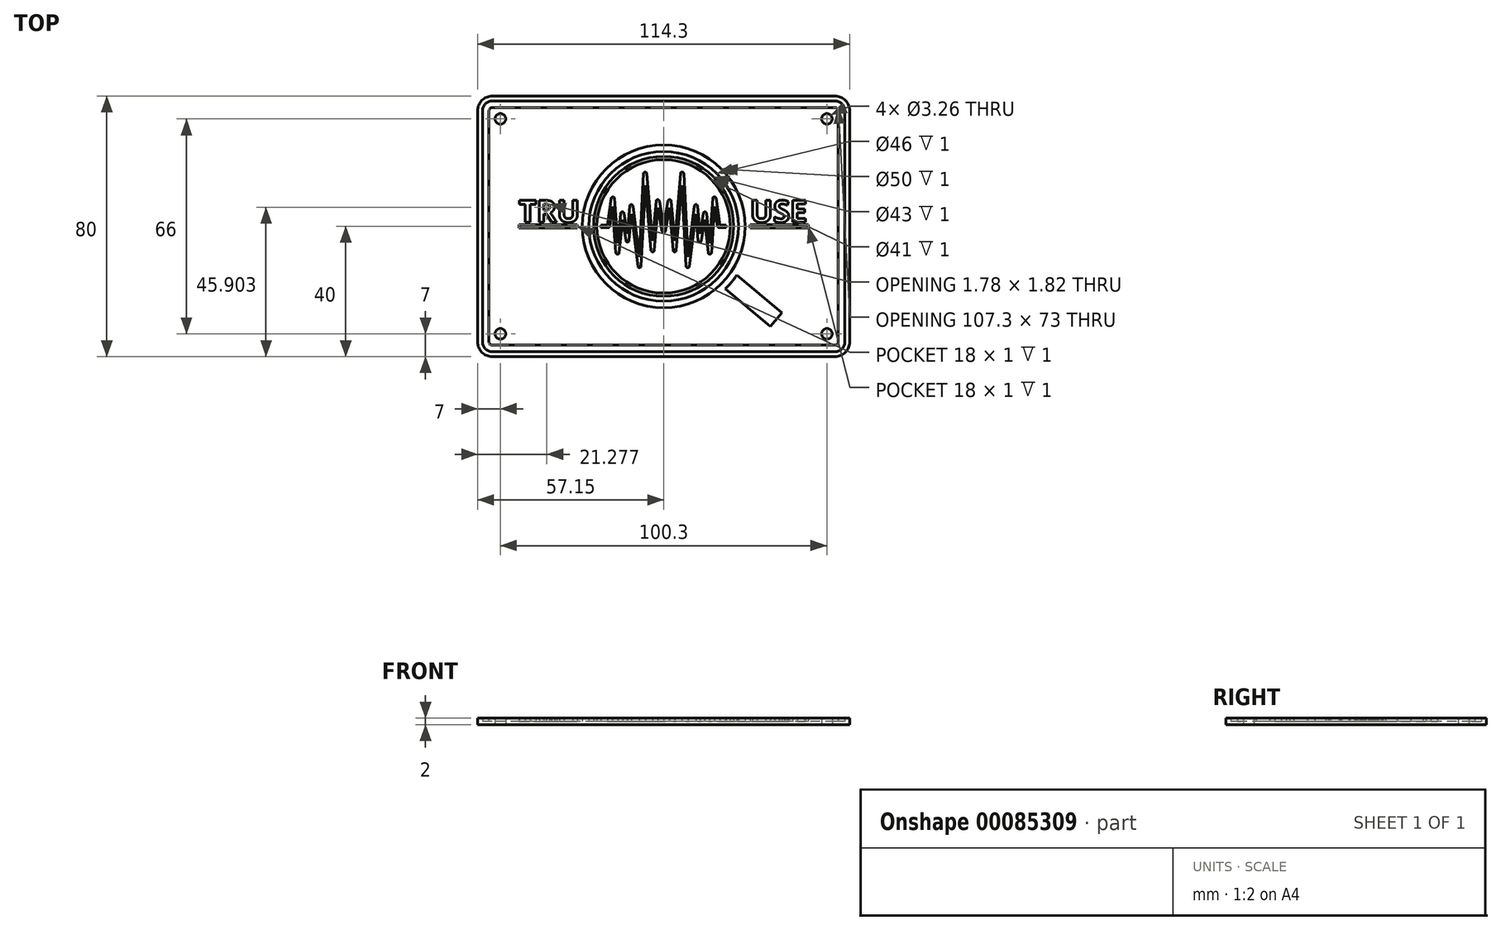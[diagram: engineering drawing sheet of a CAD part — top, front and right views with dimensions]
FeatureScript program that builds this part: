
annotation { "Feature Type Name" : "Feature", "Feature Type Description" : "" }
export const myFeature = defineFeature(function(context is Context, id is Id, definition is map)
    precondition{}
    {
        {
            var Q0;
            Q0=qCreatedBy(makeId("Front.planeOp"),FACE);
            var sketch = newSketch(context, id + "F0", { "sketchPlane" : qUnion([Q0])});
            skLineSegment(sketch, "E0.bottom", {"start": v(-57.15, 0) * mm, "end": v(57.15, 0) * mm});
            skLineSegment(sketch, "E0.top", {"start": v(-57.15, 2) * mm, "end": v(57.15, 2) * mm});
            skLineSegment(sketch, "E0.left", {"start": v(-57.15, 0) * mm, "end": v(-57.15, 2) * mm});
            skLineSegment(sketch, "E0.right", {"start": v(57.15, 0) * mm, "end": v(57.15, 2) * mm});
            skSolve(sketch);
        }
        {
            var Q0;
            Q0=makeQuery(id+"F0.imprint","IMPRINT",FACE,{"disambiguationData":[TD([[makeQuery(id+"F0.imprint","IMPRINT",EDGE,{"derivedFrom":sQuery(id+"F0.wireOp",EDGE,"E0.bottom")}),1.0]])]});
            extrude(context, id + "F1", {"entities" : qUnion([Q0]), "endBound" : BoundingType.SYMMETRIC, "depth" : 80 * mm});
        }
        {
            var Q0;
            Q0=qCreatedBy(makeId("Top.planeOp"),FACE);
            cPlane(context, id + "F2", {"entities" : qUnion([Q0]), "cplaneType" : CPlaneType.OFFSET, "offset" : 1 * mm, "width" : 150 * mm, "height" : 150 * mm});
        }
        {
            var Q0;
            Q0=qCreatedBy(id+"F2.planeOp",FACE);
            var sketch = newSketch(context, id + "F3", { "sketchPlane" : qUnion([Q0])});
            skCircle(sketch, "E1", {"center": v(0, 0) * mm, "radius": 25 * mm});
            skLineSegment(sketch, "E2.bottom", {"start": v(-44.5, -0.5) * mm, "end": v(-26.5, -0.5) * mm});
            skLineSegment(sketch, "E2.top", {"start": v(-44.5, 0.5) * mm, "end": v(-26.5, 0.5) * mm});
            skLineSegment(sketch, "E2.left", {"start": v(-44.5, -0.5) * mm, "end": v(-44.5, 0.5) * mm});
            skLineSegment(sketch, "E2.right", {"start": v(-26.5, -0.5) * mm, "end": v(-26.5, 0.5) * mm});
            skPoint(sketch, "E2.middle", {"position": v(-35.5, 0) * mm});
            skLineSegment(sketch, "E3.MirrorCS", {"start": v(44.5, 0.5) * mm, "end": v(26.5, 0.5) * mm});
            skLineSegment(sketch, "E4.MirrorCS", {"start": v(44.5, -0.5) * mm, "end": v(26.5, -0.5) * mm});
            skLineSegment(sketch, "E5.MirrorCS", {"start": v(26.5, -0.5) * mm, "end": v(26.5, 0.5) * mm});
            skLineSegment(sketch, "E6.MirrorCS", {"start": v(44.5, -0.5) * mm, "end": v(44.5, 0.5) * mm});
            skCircle(sketch, "E7", {"center": v(0, 0) * mm, "radius": 23 * mm});
            skSolve(sketch);
        }
        {
            var Q0;
            Q0=qSketchRegion(id+"F3",true);
            extrude(context, id + "F4", {"entities" : qUnion([Q0]), "depth" : 1 * mm});
        }
        {
            var Q0;
            Q0=qCreatedBy(id+"F2.planeOp",FACE);
            var sketch = newSketch(context, id + "F5", { "sketchPlane" : qUnion([Q0])});
            skCircle(sketch, "E8", {"center": v(0, 0) * mm, "radius": 21.5 * mm});
            skCircle(sketch, "E9", {"center": v(0, 0) * mm, "radius": 20.5 * mm});
            skSolve(sketch);
        }
        {
            var Q0;
            Q0=qSketchRegion(id+"F5",true);
            extrude(context, id + "F6", {"entities" : qUnion([Q0]), "depth" : 1 * mm});
        }
        {
            var Q0;
            Q0=qCreatedBy(id+"F2.planeOp",FACE);
            var sketch = newSketch(context, id + "F7", { "sketchPlane" : qUnion([Q0])});
            skLineSegment(sketch, "E10.0", {"start": v(19, -19.19) * mm, "end": v(32.78, -30.76) * mm});
            skLineSegment(sketch, "E11.0", {"start": v(22.49, -14.94) * mm, "end": v(36.32, -26.55) * mm});
            skLineSegment(sketch, "E12", {"start": v(36.32, -26.55) * mm, "end": v(32.78, -30.76) * mm});
            skArc(sketch, "E13", {"start": v(19, -19.19) * mm, "mid": v(20.85, -17.15) * mm, "end": v(22.49, -14.94) * mm});
            skSolve(sketch);
        }
        {
            var Q0;
            Q0=qSketchRegion(id+"F7",true);
            extrude(context, id + "F8", {"entities" : qUnion([Q0]), "depth" : 1 * mm});
        }
        {
            var Q0;
            Q0=qCreatedBy(id+"F2.planeOp",FACE);
            var sketch = newSketch(context, id + "F9", { "sketchPlane" : qUnion([Q0])});
            skText(sketch, "E14", { "text": "TRU", "fontName": "OpenSans-Bold.ttf"});
            skText(sketch, "E15", { "text": "USE", "fontName": "OpenSans-Bold.ttf"});
            const initialGuessF9  = {"E14": [-0.0445, 0.00125, 1, 0, 0.00679], "E15": [0.0265, 0.00125, 1, 0, 0.00678]};
            skSetInitialGuess(sketch, initialGuessF9);
            skSolve(sketch);
        }
        {
            var Q0;
            Q0=qSketchRegion(id+"F9",true);
            extrude(context, id + "F10", {"entities" : qUnion([Q0]), "depth" : 1 * mm});
        }
        {
            var Q0;
            Q0=qCreatedBy(id+"F2.planeOp",FACE);
            var sketch = newSketch(context, id + "F11", { "sketchPlane" : qUnion([Q0])});
            skPoint(sketch, "E16.middle", {"position": v(0, 0) * mm});
            skLineSegment(sketch, "E17.bottom", {"start": v(52.65, 38.5) * mm, "end": v(-52.65, 38.5) * mm});
            skLineSegment(sketch, "E17.top", {"start": v(52.65, -38.5) * mm, "end": v(-52.65, -38.5) * mm});
            skLineSegment(sketch, "E17.left", {"start": v(55.65, 35.5) * mm, "end": v(55.65, -35.5) * mm});
            skLineSegment(sketch, "E17.right", {"start": v(-55.65, 35.5) * mm, "end": v(-55.65, -35.5) * mm});
            skLineSegment(sketch, "E18.bottom", {"start": v(52.65, 36.5) * mm, "end": v(-52.65, 36.5) * mm});
            skLineSegment(sketch, "E18.top", {"start": v(52.65, -36.5) * mm, "end": v(-52.65, -36.5) * mm});
            skLineSegment(sketch, "E18.left", {"start": v(53.65, 35.5) * mm, "end": v(53.65, -35.5) * mm});
            skLineSegment(sketch, "E18.right", {"start": v(-53.65, 35.5) * mm, "end": v(-53.65, -35.5) * mm});
            skPoint(sketch, "E19.visualSharp", {"position": v(-55.65, 38.5) * mm});
            skArc(sketch, "E19.filletArc", {"start": v(-52.65, 38.5) * mm, "mid": v(-54.77, 37.62) * mm, "end": v(-55.65, 35.5) * mm});
            skPoint(sketch, "E20.visualSharp", {"position": v(55.65, 38.5) * mm});
            skArc(sketch, "E20.filletArc", {"start": v(55.65, 35.5) * mm, "mid": v(54.77, 37.62) * mm, "end": v(52.65, 38.5) * mm});
            skPoint(sketch, "E21.visualSharp", {"position": v(55.65, -38.5) * mm});
            skArc(sketch, "E21.filletArc", {"start": v(52.65, -38.5) * mm, "mid": v(54.77, -37.62) * mm, "end": v(55.65, -35.5) * mm});
            skPoint(sketch, "E22.visualSharp", {"position": v(-55.65, -38.5) * mm});
            skArc(sketch, "E22.filletArc", {"start": v(-55.65, -35.5) * mm, "mid": v(-54.77, -37.62) * mm, "end": v(-52.65, -38.5) * mm});
            skPoint(sketch, "E23.visualSharp", {"position": v(53.65, 36.5) * mm});
            skArc(sketch, "E23.filletArc", {"start": v(53.65, 35.5) * mm, "mid": v(53.36, 36.2) * mm, "end": v(52.65, 36.5) * mm});
            skPoint(sketch, "E24.visualSharp", {"position": v(-53.65, 36.5) * mm});
            skArc(sketch, "E24.filletArc", {"start": v(-52.65, 36.5) * mm, "mid": v(-53.36, 36.2) * mm, "end": v(-53.65, 35.5) * mm});
            skPoint(sketch, "E25.visualSharp", {"position": v(-53.65, -36.5) * mm});
            skArc(sketch, "E25.filletArc", {"start": v(-53.65, -35.5) * mm, "mid": v(-53.36, -36.2) * mm, "end": v(-52.65, -36.5) * mm});
            skPoint(sketch, "E26.visualSharp", {"position": v(53.65, -36.5) * mm});
            skArc(sketch, "E26.filletArc", {"start": v(52.65, -36.5) * mm, "mid": v(53.36, -36.2) * mm, "end": v(53.65, -35.5) * mm});
            skSolve(sketch);
        }
        {
            var Q0;
            Q0=qSketchRegion(id+"F11",true);
            extrude(context, id + "F12", {"entities" : qUnion([Q0]), "depth" : 1 * mm});
        }
        {
            var Q0;
            Q0=qCreatedBy(id+"F2.planeOp",FACE);
            var sketch = newSketch(context, id + "F13", { "sketchPlane" : qUnion([Q0])});
            skLineSegment(sketch, "E27.bottom", {"start": v(-17.03, -0.38) * mm, "end": v(-19.25, -0.37) * mm});
            skLineSegment(sketch, "E27.top", {"start": v(-17.25, 0.38) * mm, "end": v(-19.25, 0.38) * mm});
            skLineSegment(sketch, "E27.right", {"start": v(-19.25, -0.37) * mm, "end": v(-19.25, 0.38) * mm});
            skPoint(sketch, "E27.middle", {"position": v(-18.25, 0) * mm});
            skLineSegment(sketch, "E28", {"start": v(-17.25, 0.37) * mm, "end": v(-16.09, 8.62) * mm});
            skLineSegment(sketch, "E29.0", {"start": v(-16.53, 0.06) * mm, "end": v(-15.68, 6.16) * mm});
            skPoint(sketch, "E27.left.start.orphan", {"position": v(-17.25, -0.38) * mm});
            skPoint(sketch, "E30.visualSharp", {"position": v(-16.6, -0.38) * mm});
            skArc(sketch, "E30.filletArc", {"start": v(-17.03, -0.38) * mm, "mid": v(-16.7, -0.25) * mm, "end": v(-16.53, 0.06) * mm});
            skLineSegment(sketch, "E31", {"start": v(-15.68, 6.16) * mm, "end": v(-14.68, -8.1) * mm});
            skLineSegment(sketch, "E32.0", {"start": v(-15.1, 8.58) * mm, "end": v(-14.13, -5.19) * mm});
            skPoint(sketch, "E33.visualSharp", {"position": v(-15.43, 13.33) * mm});
            skArc(sketch, "E33.filletArc", {"start": v(-15.1, 8.58) * mm, "mid": v(-15.58, 9.05) * mm, "end": v(-16.09, 8.62) * mm});
            skLineSegment(sketch, "E34", {"start": v(-14.13, -5.19) * mm, "end": v(-13.16, 4) * mm});
            skLineSegment(sketch, "E35.0", {"start": v(-13.68, -8.1) * mm, "end": v(-12.62, 2.03) * mm});
            skLineSegment(sketch, "E36", {"start": v(-12.62, 2.03) * mm, "end": v(-11.6, -4.4) * mm});
            skLineSegment(sketch, "E37.0", {"start": v(-12.17, 4.02) * mm, "end": v(-11.18, -2.27) * mm});
            skLineSegment(sketch, "E38", {"start": v(-11.18, -2.27) * mm, "end": v(-10.43, 6.22) * mm});
            skLineSegment(sketch, "E39.0", {"start": v(-10.6, -4.37) * mm, "end": v(-9.9, 3.78) * mm});
            skLineSegment(sketch, "E40", {"start": v(-9.9, 3.78) * mm, "end": v(-7.92, -12.26) * mm});
            skLineSegment(sketch, "E41.0", {"start": v(-9.44, 6.24) * mm, "end": v(-7.53, -9.33) * mm});
            skLineSegment(sketch, "E42", {"start": v(-7.53, -9.33) * mm, "end": v(-6.19, 16.22) * mm});
            skLineSegment(sketch, "E43.0", {"start": v(-6.93, -12.22) * mm, "end": v(-5.63, 12.61) * mm});
            skLineSegment(sketch, "E44", {"start": v(-5.63, 12.61) * mm, "end": v(-3.88, -7.38) * mm});
            skLineSegment(sketch, "E45.0", {"start": v(-5.2, 16.24) * mm, "end": v(-3.38, -4.47) * mm});
            skLineSegment(sketch, "E46", {"start": v(-3.38, -4.47) * mm, "end": v(-2.31, 7.74) * mm});
            skLineSegment(sketch, "E47.0", {"start": v(-2.88, -7.38) * mm, "end": v(-1.73, 5.74) * mm});
            skLineSegment(sketch, "E48", {"start": v(0, 12.7) * mm, "end": v(0, -16.33) * mm, "construction": true});
            skLineSegment(sketch, "E49", {"start": v(-1.73, 5.74) * mm, "end": v(-0.5, -1.53) * mm});
            skLineSegment(sketch, "E50.0", {"start": v(-1.32, 7.78) * mm, "end": v(0, 0.04) * mm});
            skPoint(sketch, "E51.visualSharp", {"position": v(-14.28, -13.8) * mm});
            skArc(sketch, "E51.filletArc", {"start": v(-14.68, -8.1) * mm, "mid": v(-14.19, -8.56) * mm, "end": v(-13.68, -8.1) * mm});
            skPoint(sketch, "E52.visualSharp", {"position": v(-12.77, 7.78) * mm});
            skArc(sketch, "E52.filletArc", {"start": v(-12.17, 4.02) * mm, "mid": v(-12.68, 4.45) * mm, "end": v(-13.16, 4) * mm});
            skPoint(sketch, "E53.visualSharp", {"position": v(-10.96, -8.42) * mm});
            skArc(sketch, "E53.filletArc", {"start": v(-11.6, -4.4) * mm, "mid": v(-11.09, -4.82) * mm, "end": v(-10.6, -4.37) * mm});
            skPoint(sketch, "E54.visualSharp", {"position": v(-10.02, 10.96) * mm});
            skArc(sketch, "E54.filletArc", {"start": v(-9.44, 6.24) * mm, "mid": v(-9.94, 6.67) * mm, "end": v(-10.43, 6.22) * mm});
            skPoint(sketch, "E55.visualSharp", {"position": v(-7.23, -17.93) * mm});
            skArc(sketch, "E55.filletArc", {"start": v(-7.92, -12.26) * mm, "mid": v(-7.4, -12.7) * mm, "end": v(-6.93, -12.22) * mm});
            skPoint(sketch, "E56.visualSharp", {"position": v(-5.81, 23.36) * mm});
            skArc(sketch, "E56.filletArc", {"start": v(-5.2, 16.24) * mm, "mid": v(-5.7, 16.7) * mm, "end": v(-6.19, 16.22) * mm});
            skPoint(sketch, "E57.visualSharp", {"position": v(-3.38, -13.07) * mm});
            skArc(sketch, "E57.filletArc", {"start": v(-3.88, -7.38) * mm, "mid": v(-3.38, -7.84) * mm, "end": v(-2.88, -7.38) * mm});
            skPoint(sketch, "E58.visualSharp", {"position": v(-1.97, 11.61) * mm});
            skArc(sketch, "E58.filletArc", {"start": v(-1.32, 7.78) * mm, "mid": v(-1.83, 8.2) * mm, "end": v(-2.31, 7.74) * mm});
            skArc(sketch, "E59.MirrorCS", {"start": v(17.03, -0.38) * mm, "mid": v(16.7, -0.25) * mm, "end": v(16.53, 0.06) * mm});
            skArc(sketch, "E60.MirrorCS", {"start": v(5.2, 16.24) * mm, "mid": v(5.7, 16.7) * mm, "end": v(6.19, 16.22) * mm});
            skArc(sketch, "E61.MirrorCS", {"start": v(1.32, 7.78) * mm, "mid": v(1.83, 8.2) * mm, "end": v(2.31, 7.74) * mm});
            skArc(sketch, "E62.MirrorCS", {"start": v(3.88, -7.38) * mm, "mid": v(3.38, -7.84) * mm, "end": v(2.88, -7.38) * mm});
            skArc(sketch, "E63.MirrorCS", {"start": v(14.68, -8.1) * mm, "mid": v(14.19, -8.56) * mm, "end": v(13.68, -8.1) * mm});
            skArc(sketch, "E64.MirrorCS", {"start": v(11.6, -4.4) * mm, "mid": v(11.09, -4.82) * mm, "end": v(10.6, -4.37) * mm});
            skArc(sketch, "E65.MirrorCS", {"start": v(9.44, 6.24) * mm, "mid": v(9.94, 6.67) * mm, "end": v(10.43, 6.22) * mm});
            skArc(sketch, "E66.MirrorCS", {"start": v(15.1, 8.58) * mm, "mid": v(15.58, 9.05) * mm, "end": v(16.09, 8.62) * mm});
            skArc(sketch, "E67.MirrorCS", {"start": v(12.17, 4.02) * mm, "mid": v(12.68, 4.45) * mm, "end": v(13.16, 4) * mm});
            skArc(sketch, "E68.MirrorCS", {"start": v(7.92, -12.26) * mm, "mid": v(7.4, -12.7) * mm, "end": v(6.93, -12.22) * mm});
            skLineSegment(sketch, "E69.MirrorCS", {"start": v(19.25, -0.37) * mm, "end": v(19.25, 0.38) * mm});
            skLineSegment(sketch, "E70.MirrorCS", {"start": v(17.03, -0.38) * mm, "end": v(19.25, -0.37) * mm});
            skPoint(sketch, "E71.MirrorP", {"position": v(16.6, -0.38) * mm});
            skLineSegment(sketch, "E72.MirrorCS", {"start": v(17.25, 0.38) * mm, "end": v(19.25, 0.38) * mm});
            skPoint(sketch, "E73.MirrorP", {"position": v(17.25, -0.38) * mm});
            skPoint(sketch, "E74.MirrorP", {"position": v(18.25, 0) * mm});
            skLineSegment(sketch, "E75.MirrorCS", {"start": v(7.53, -9.33) * mm, "end": v(6.19, 16.22) * mm});
            skPoint(sketch, "E76.MirrorP", {"position": v(12.77, 7.78) * mm});
            skLineSegment(sketch, "E77.MirrorCS", {"start": v(3.38, -4.47) * mm, "end": v(2.31, 7.74) * mm});
            skLineSegment(sketch, "E78.MirrorCS", {"start": v(12.17, 4.02) * mm, "end": v(11.18, -2.27) * mm});
            skLineSegment(sketch, "E79.MirrorCS", {"start": v(1.73, 5.74) * mm, "end": v(0.5, -1.53) * mm});
            skPoint(sketch, "E80.MirrorP", {"position": v(14.28, -13.8) * mm});
            skLineSegment(sketch, "E81.MirrorCS", {"start": v(1.32, 7.78) * mm, "end": v(0, 0.04) * mm});
            skLineSegment(sketch, "E82.MirrorCS", {"start": v(10.6, -4.37) * mm, "end": v(9.9, 3.78) * mm});
            skLineSegment(sketch, "E83.MirrorCS", {"start": v(9.9, 3.78) * mm, "end": v(7.92, -12.26) * mm});
            skPoint(sketch, "E84.MirrorP", {"position": v(10.96, -8.42) * mm});
            skLineSegment(sketch, "E85.MirrorCS", {"start": v(9.44, 6.24) * mm, "end": v(7.53, -9.33) * mm});
            skLineSegment(sketch, "E86.MirrorCS", {"start": v(2.88, -7.38) * mm, "end": v(1.73, 5.74) * mm});
            skLineSegment(sketch, "E87.MirrorCS", {"start": v(12.62, 2.03) * mm, "end": v(11.6, -4.4) * mm});
            skPoint(sketch, "E88.MirrorP", {"position": v(1.97, 11.61) * mm});
            skPoint(sketch, "E89.MirrorP", {"position": v(3.38, -13.07) * mm});
            skPoint(sketch, "E90.MirrorP", {"position": v(15.43, 13.33) * mm});
            skPoint(sketch, "E91.MirrorP", {"position": v(10.02, 10.96) * mm});
            skLineSegment(sketch, "E92.MirrorCS", {"start": v(5.2, 16.24) * mm, "end": v(3.38, -4.47) * mm});
            skLineSegment(sketch, "E93.MirrorCS", {"start": v(17.25, 0.37) * mm, "end": v(16.09, 8.62) * mm});
            skLineSegment(sketch, "E94.MirrorCS", {"start": v(5.63, 12.61) * mm, "end": v(3.88, -7.38) * mm});
            skLineSegment(sketch, "E95.MirrorCS", {"start": v(14.13, -5.19) * mm, "end": v(13.16, 4) * mm});
            skLineSegment(sketch, "E96.MirrorCS", {"start": v(13.68, -8.1) * mm, "end": v(12.62, 2.03) * mm});
            skLineSegment(sketch, "E97.MirrorCS", {"start": v(15.68, 6.16) * mm, "end": v(14.68, -8.1) * mm});
            skLineSegment(sketch, "E98.MirrorCS", {"start": v(6.93, -12.22) * mm, "end": v(5.63, 12.61) * mm});
            skLineSegment(sketch, "E99.MirrorCS", {"start": v(15.1, 8.58) * mm, "end": v(14.13, -5.19) * mm});
            skLineSegment(sketch, "E100.MirrorCS", {"start": v(16.53, 0.06) * mm, "end": v(15.68, 6.16) * mm});
            skLineSegment(sketch, "E101.MirrorCS", {"start": v(11.18, -2.27) * mm, "end": v(10.43, 6.22) * mm});
            skPoint(sketch, "E102.visualSharp", {"position": v(0, -4.42) * mm});
            skArc(sketch, "E102.filletArc", {"start": v(-0.5, -1.53) * mm, "mid": v(0, -1.95) * mm, "end": v(0.5, -1.53) * mm});
            skSolve(sketch);
        }
        {
            var Q0;
            Q0=qSketchRegion(id+"F13",true);
            extrude(context, id + "F14", {"entities" : qUnion([Q0]), "depth" : 1 * mm});
        }
        {
            var Q0;
            Q0=makeQuery(id+"F1.opExtrude","CAP_EDGE",EDGE,{"disambiguationData":[OSD([sQuery(id+"F0.wireOp",EDGE,"E0.right")])],"isStart":true});
            var Q1;
            Q1=makeQuery(id+"F1.opExtrude","CAP_EDGE",EDGE,{"disambiguationData":[OSD([sQuery(id+"F0.wireOp",EDGE,"E0.right")])],"isStart":false});
            var Q2;
            Q2=makeQuery(id+"F1.opExtrude","CAP_EDGE",EDGE,{"disambiguationData":[OSD([sQuery(id+"F0.wireOp",EDGE,"E0.left")])],"isStart":false});
            var Q3;
            Q3=makeQuery(id+"F1.opExtrude","CAP_EDGE",EDGE,{"disambiguationData":[OSD([sQuery(id+"F0.wireOp",EDGE,"E0.left")])],"isStart":true});
            fillet(context, id + "F15", {"entities" : qUnion([Q0, Q1, Q2, Q3]), "radius" : 4.5 * mm, "tangentPropagation" : true, "allowEdgeOverflow" : false});
        }
        {
            var Q0;
            Q0=makeQuery(id+"F14.opExtrude","SWEPT_BODY",BODY,{"disambiguationData":[OSD([sQuery(id+"F13.wireOp",EDGE,"E27.bottom"),sQuery(id+"F13.wireOp",EDGE,"E27.top"),sQuery(id+"F13.wireOp",EDGE,"E27.right"),sQuery(id+"F13.wireOp",EDGE,"E28"),sQuery(id+"F13.wireOp",EDGE,"E29.0"),sQuery(id+"F13.wireOp",EDGE,"E30.filletArc"),sQuery(id+"F13.wireOp",EDGE,"E31"),sQuery(id+"F13.wireOp",EDGE,"E32.0"),sQuery(id+"F13.wireOp",EDGE,"E33.filletArc"),sQuery(id+"F13.wireOp",EDGE,"E34"),sQuery(id+"F13.wireOp",EDGE,"E35.0"),sQuery(id+"F13.wireOp",EDGE,"E36"),sQuery(id+"F13.wireOp",EDGE,"E37.0"),sQuery(id+"F13.wireOp",EDGE,"E38"),sQuery(id+"F13.wireOp",EDGE,"E39.0"),sQuery(id+"F13.wireOp",EDGE,"E40"),sQuery(id+"F13.wireOp",EDGE,"E41.0"),sQuery(id+"F13.wireOp",EDGE,"E42"),sQuery(id+"F13.wireOp",EDGE,"E43.0"),sQuery(id+"F13.wireOp",EDGE,"E44"),sQuery(id+"F13.wireOp",EDGE,"E45.0"),sQuery(id+"F13.wireOp",EDGE,"E46"),sQuery(id+"F13.wireOp",EDGE,"E47.0"),sQuery(id+"F13.wireOp",EDGE,"E49"),sQuery(id+"F13.wireOp",EDGE,"E50.0"),sQuery(id+"F13.wireOp",EDGE,"E51.filletArc"),sQuery(id+"F13.wireOp",EDGE,"E52.filletArc"),sQuery(id+"F13.wireOp",EDGE,"E53.filletArc"),sQuery(id+"F13.wireOp",EDGE,"E54.filletArc"),sQuery(id+"F13.wireOp",EDGE,"E55.filletArc"),sQuery(id+"F13.wireOp",EDGE,"E56.filletArc"),sQuery(id+"F13.wireOp",EDGE,"E57.filletArc"),sQuery(id+"F13.wireOp",EDGE,"E58.filletArc"),sQuery(id+"F13.wireOp",EDGE,"E59.MirrorCS"),sQuery(id+"F13.wireOp",EDGE,"E60.MirrorCS"),sQuery(id+"F13.wireOp",EDGE,"E61.MirrorCS"),sQuery(id+"F13.wireOp",EDGE,"E62.MirrorCS"),sQuery(id+"F13.wireOp",EDGE,"E63.MirrorCS"),sQuery(id+"F13.wireOp",EDGE,"E64.MirrorCS"),sQuery(id+"F13.wireOp",EDGE,"E65.MirrorCS"),sQuery(id+"F13.wireOp",EDGE,"E66.MirrorCS"),sQuery(id+"F13.wireOp",EDGE,"E67.MirrorCS"),sQuery(id+"F13.wireOp",EDGE,"E68.MirrorCS"),sQuery(id+"F13.wireOp",EDGE,"E69.MirrorCS"),sQuery(id+"F13.wireOp",EDGE,"E70.MirrorCS"),sQuery(id+"F13.wireOp",EDGE,"E72.MirrorCS"),sQuery(id+"F13.wireOp",EDGE,"E75.MirrorCS"),sQuery(id+"F13.wireOp",EDGE,"E77.MirrorCS"),sQuery(id+"F13.wireOp",EDGE,"E78.MirrorCS"),sQuery(id+"F13.wireOp",EDGE,"E79.MirrorCS"),sQuery(id+"F13.wireOp",EDGE,"E81.MirrorCS"),sQuery(id+"F13.wireOp",EDGE,"E82.MirrorCS"),sQuery(id+"F13.wireOp",EDGE,"E83.MirrorCS"),sQuery(id+"F13.wireOp",EDGE,"E85.MirrorCS"),sQuery(id+"F13.wireOp",EDGE,"E86.MirrorCS"),sQuery(id+"F13.wireOp",EDGE,"E87.MirrorCS"),sQuery(id+"F13.wireOp",EDGE,"E92.MirrorCS"),sQuery(id+"F13.wireOp",EDGE,"E93.MirrorCS"),sQuery(id+"F13.wireOp",EDGE,"E94.MirrorCS"),sQuery(id+"F13.wireOp",EDGE,"E95.MirrorCS"),sQuery(id+"F13.wireOp",EDGE,"E96.MirrorCS"),sQuery(id+"F13.wireOp",EDGE,"E97.MirrorCS"),sQuery(id+"F13.wireOp",EDGE,"E98.MirrorCS"),sQuery(id+"F13.wireOp",EDGE,"E99.MirrorCS"),sQuery(id+"F13.wireOp",EDGE,"E100.MirrorCS"),sQuery(id+"F13.wireOp",EDGE,"E101.MirrorCS"),sQuery(id+"F13.wireOp",EDGE,"E102.filletArc")])]});
            var Q1;
            Q1=makeQuery(id+"F1.opExtrude","SWEPT_BODY",BODY,{"disambiguationData":[OSD([sQuery(id+"F0.wireOp",EDGE,"E0.bottom"),sQuery(id+"F0.wireOp",EDGE,"E0.top"),sQuery(id+"F0.wireOp",EDGE,"E0.left"),sQuery(id+"F0.wireOp",EDGE,"E0.right")])]});
            booleanBodies(context, id + "F16", {"operationType" : BooleanOperationType.SUBTRACTION, "tools" : qUnion([Q0]), "targets" : qUnion([Q1]), "keepTools" : true});
        }
        {
            var Q0;
            Q0=makeQuery(id+"F4.opExtrude","SWEPT_BODY",BODY,{"disambiguationData":[OSD([sQuery(id+"F3.wireOp",EDGE,"E1"),sQuery(id+"F3.wireOp",EDGE,"E7")])]});
            var Q1;
            Q1=makeQuery(id+"F4.opExtrude","SWEPT_BODY",BODY,{"disambiguationData":[OSD([sQuery(id+"F3.wireOp",EDGE,"E2.bottom"),sQuery(id+"F3.wireOp",EDGE,"E2.top"),sQuery(id+"F3.wireOp",EDGE,"E2.left"),sQuery(id+"F3.wireOp",EDGE,"E2.right")])]});
            var Q2;
            Q2=makeQuery(id+"F4.opExtrude","SWEPT_BODY",BODY,{"disambiguationData":[OSD([sQuery(id+"F3.wireOp",EDGE,"E3.MirrorCS"),sQuery(id+"F3.wireOp",EDGE,"E4.MirrorCS"),sQuery(id+"F3.wireOp",EDGE,"E5.MirrorCS"),sQuery(id+"F3.wireOp",EDGE,"E6.MirrorCS")])]});
            var Q3;
            Q3=makeQuery(id+"F1.opExtrude","SWEPT_BODY",BODY,{"disambiguationData":[OSD([sQuery(id+"F0.wireOp",EDGE,"E0.bottom"),sQuery(id+"F0.wireOp",EDGE,"E0.top"),sQuery(id+"F0.wireOp",EDGE,"E0.left"),sQuery(id+"F0.wireOp",EDGE,"E0.right")])]});
            booleanBodies(context, id + "F17", {"operationType" : BooleanOperationType.SUBTRACTION, "tools" : qUnion([Q0, Q1, Q2]), "targets" : qUnion([Q3]), "keepTools" : true});
        }
        {
            var Q0;
            Q0=makeQuery(id+"F6.opExtrude","SWEPT_BODY",BODY,{"disambiguationData":[OSD([sQuery(id+"F5.wireOp",EDGE,"E8"),sQuery(id+"F5.wireOp",EDGE,"E9")])]});
            var Q1;
            Q1=makeQuery(id+"F1.opExtrude","SWEPT_BODY",BODY,{"disambiguationData":[OSD([sQuery(id+"F0.wireOp",EDGE,"E0.bottom"),sQuery(id+"F0.wireOp",EDGE,"E0.top"),sQuery(id+"F0.wireOp",EDGE,"E0.left"),sQuery(id+"F0.wireOp",EDGE,"E0.right")])]});
            booleanBodies(context, id + "F18", {"operationType" : BooleanOperationType.SUBTRACTION, "tools" : qUnion([Q0]), "targets" : qUnion([Q1]), "keepTools" : true});
        }
        {
            var Q0;
            Q0=makeQuery(id+"F8.opExtrude","SWEPT_BODY",BODY,{"disambiguationData":[OSD([sQuery(id+"F7.wireOp",EDGE,"E10.0"),sQuery(id+"F7.wireOp",EDGE,"E11.0"),sQuery(id+"F7.wireOp",EDGE,"E12"),sQuery(id+"F7.wireOp",EDGE,"E13")])]});
            var Q1;
            Q1=makeQuery(id+"F1.opExtrude","SWEPT_BODY",BODY,{"disambiguationData":[OSD([sQuery(id+"F0.wireOp",EDGE,"E0.bottom"),sQuery(id+"F0.wireOp",EDGE,"E0.top"),sQuery(id+"F0.wireOp",EDGE,"E0.left"),sQuery(id+"F0.wireOp",EDGE,"E0.right")])]});
            booleanBodies(context, id + "F19", {"operationType" : BooleanOperationType.SUBTRACTION, "tools" : qUnion([Q0]), "targets" : qUnion([Q1]), "keepTools" : true});
        }
        {
            var Q0;
            Q0=makeQuery(id+"F10.opExtrude","SWEPT_BODY",BODY,{"disambiguationData":[OSD([sQuery(id+"F9.wireOp",EDGE,"E14.sketch_text.stroke-0"),sQuery(id+"F9.wireOp",EDGE,"E14.sketch_text.stroke-1"),sQuery(id+"F9.wireOp",EDGE,"E14.sketch_text.stroke-2"),sQuery(id+"F9.wireOp",EDGE,"E14.sketch_text.stroke-3"),sQuery(id+"F9.wireOp",EDGE,"E14.sketch_text.stroke-4"),sQuery(id+"F9.wireOp",EDGE,"E14.sketch_text.stroke-5"),sQuery(id+"F9.wireOp",EDGE,"E14.sketch_text.stroke-6"),sQuery(id+"F9.wireOp",EDGE,"E14.sketch_text.stroke-7")])]});
            var Q1;
            Q1=makeQuery(id+"F10.opExtrude","SWEPT_BODY",BODY,{"disambiguationData":[OSD([sQuery(id+"F9.wireOp",EDGE,"E14.sketch_text.stroke-8"),sQuery(id+"F9.wireOp",EDGE,"E14.sketch_text.stroke-9"),sQuery(id+"F9.wireOp",EDGE,"E14.sketch_text.stroke-10"),sQuery(id+"F9.wireOp",EDGE,"E14.sketch_text.stroke-11"),sQuery(id+"F9.wireOp",EDGE,"E14.sketch_text.stroke-12"),sQuery(id+"F9.wireOp",EDGE,"E14.sketch_text.stroke-13"),sQuery(id+"F9.wireOp",EDGE,"E14.sketch_text.stroke-14"),sQuery(id+"F9.wireOp",EDGE,"E14.sketch_text.stroke-15"),sQuery(id+"F9.wireOp",EDGE,"E14.sketch_text.stroke-16"),sQuery(id+"F9.wireOp",EDGE,"E14.sketch_text.stroke-17"),sQuery(id+"F9.wireOp",EDGE,"E14.sketch_text.stroke-18"),sQuery(id+"F9.wireOp",EDGE,"E14.sketch_text.stroke-19"),sQuery(id+"F9.wireOp",EDGE,"E14.sketch_text.stroke-20"),sQuery(id+"F9.wireOp",EDGE,"E14.sketch_text.stroke-21"),sQuery(id+"F9.wireOp",EDGE,"E14.sketch_text.stroke-22"),sQuery(id+"F9.wireOp",EDGE,"E14.sketch_text.stroke-23"),sQuery(id+"F9.wireOp",EDGE,"E14.sketch_text.stroke-24"),sQuery(id+"F9.wireOp",EDGE,"E14.sketch_text.stroke-25"),sQuery(id+"F9.wireOp",EDGE,"E14.sketch_text.stroke-26")])]});
            var Q2;
            Q2=makeQuery(id+"F10.opExtrude","SWEPT_BODY",BODY,{"disambiguationData":[OSD([sQuery(id+"F9.wireOp",EDGE,"E14.sketch_text.stroke-27"),sQuery(id+"F9.wireOp",EDGE,"E14.sketch_text.stroke-28"),sQuery(id+"F9.wireOp",EDGE,"E14.sketch_text.stroke-29"),sQuery(id+"F9.wireOp",EDGE,"E14.sketch_text.stroke-30"),sQuery(id+"F9.wireOp",EDGE,"E14.sketch_text.stroke-31"),sQuery(id+"F9.wireOp",EDGE,"E14.sketch_text.stroke-32"),sQuery(id+"F9.wireOp",EDGE,"E14.sketch_text.stroke-33"),sQuery(id+"F9.wireOp",EDGE,"E14.sketch_text.stroke-34"),sQuery(id+"F9.wireOp",EDGE,"E14.sketch_text.stroke-35"),sQuery(id+"F9.wireOp",EDGE,"E14.sketch_text.stroke-36"),sQuery(id+"F9.wireOp",EDGE,"E14.sketch_text.stroke-37"),sQuery(id+"F9.wireOp",EDGE,"E14.sketch_text.stroke-38"),sQuery(id+"F9.wireOp",EDGE,"E14.sketch_text.stroke-39"),sQuery(id+"F9.wireOp",EDGE,"E14.sketch_text.stroke-40"),sQuery(id+"F9.wireOp",EDGE,"E14.sketch_text.stroke-41")])]});
            var Q3;
            Q3=makeQuery(id+"F10.opExtrude","SWEPT_BODY",BODY,{"disambiguationData":[OSD([sQuery(id+"F9.wireOp",EDGE,"E15.sketch_text.stroke-0"),sQuery(id+"F9.wireOp",EDGE,"E15.sketch_text.stroke-1"),sQuery(id+"F9.wireOp",EDGE,"E15.sketch_text.stroke-2"),sQuery(id+"F9.wireOp",EDGE,"E15.sketch_text.stroke-3"),sQuery(id+"F9.wireOp",EDGE,"E15.sketch_text.stroke-4"),sQuery(id+"F9.wireOp",EDGE,"E15.sketch_text.stroke-5"),sQuery(id+"F9.wireOp",EDGE,"E15.sketch_text.stroke-6"),sQuery(id+"F9.wireOp",EDGE,"E15.sketch_text.stroke-7"),sQuery(id+"F9.wireOp",EDGE,"E15.sketch_text.stroke-8"),sQuery(id+"F9.wireOp",EDGE,"E15.sketch_text.stroke-9"),sQuery(id+"F9.wireOp",EDGE,"E15.sketch_text.stroke-10"),sQuery(id+"F9.wireOp",EDGE,"E15.sketch_text.stroke-11"),sQuery(id+"F9.wireOp",EDGE,"E15.sketch_text.stroke-12"),sQuery(id+"F9.wireOp",EDGE,"E15.sketch_text.stroke-13"),sQuery(id+"F9.wireOp",EDGE,"E15.sketch_text.stroke-14")])]});
            var Q4;
            Q4=makeQuery(id+"F10.opExtrude","SWEPT_BODY",BODY,{"disambiguationData":[OSD([sQuery(id+"F9.wireOp",EDGE,"E15.sketch_text.stroke-15"),sQuery(id+"F9.wireOp",EDGE,"E15.sketch_text.stroke-16"),sQuery(id+"F9.wireOp",EDGE,"E15.sketch_text.stroke-17"),sQuery(id+"F9.wireOp",EDGE,"E15.sketch_text.stroke-18"),sQuery(id+"F9.wireOp",EDGE,"E15.sketch_text.stroke-19"),sQuery(id+"F9.wireOp",EDGE,"E15.sketch_text.stroke-20"),sQuery(id+"F9.wireOp",EDGE,"E15.sketch_text.stroke-21"),sQuery(id+"F9.wireOp",EDGE,"E15.sketch_text.stroke-22"),sQuery(id+"F9.wireOp",EDGE,"E15.sketch_text.stroke-23"),sQuery(id+"F9.wireOp",EDGE,"E15.sketch_text.stroke-24"),sQuery(id+"F9.wireOp",EDGE,"E15.sketch_text.stroke-25"),sQuery(id+"F9.wireOp",EDGE,"E15.sketch_text.stroke-26"),sQuery(id+"F9.wireOp",EDGE,"E15.sketch_text.stroke-27"),sQuery(id+"F9.wireOp",EDGE,"E15.sketch_text.stroke-28"),sQuery(id+"F9.wireOp",EDGE,"E15.sketch_text.stroke-29"),sQuery(id+"F9.wireOp",EDGE,"E15.sketch_text.stroke-30"),sQuery(id+"F9.wireOp",EDGE,"E15.sketch_text.stroke-31"),sQuery(id+"F9.wireOp",EDGE,"E15.sketch_text.stroke-32"),sQuery(id+"F9.wireOp",EDGE,"E15.sketch_text.stroke-33"),sQuery(id+"F9.wireOp",EDGE,"E15.sketch_text.stroke-34"),sQuery(id+"F9.wireOp",EDGE,"E15.sketch_text.stroke-35"),sQuery(id+"F9.wireOp",EDGE,"E15.sketch_text.stroke-36"),sQuery(id+"F9.wireOp",EDGE,"E15.sketch_text.stroke-37"),sQuery(id+"F9.wireOp",EDGE,"E15.sketch_text.stroke-38"),sQuery(id+"F9.wireOp",EDGE,"E15.sketch_text.stroke-39"),sQuery(id+"F9.wireOp",EDGE,"E15.sketch_text.stroke-40"),sQuery(id+"F9.wireOp",EDGE,"E15.sketch_text.stroke-41"),sQuery(id+"F9.wireOp",EDGE,"E15.sketch_text.stroke-42")])]});
            var Q5;
            Q5=makeQuery(id+"F10.opExtrude","SWEPT_BODY",BODY,{"disambiguationData":[OSD([sQuery(id+"F9.wireOp",EDGE,"E15.sketch_text.stroke-43"),sQuery(id+"F9.wireOp",EDGE,"E15.sketch_text.stroke-44"),sQuery(id+"F9.wireOp",EDGE,"E15.sketch_text.stroke-45"),sQuery(id+"F9.wireOp",EDGE,"E15.sketch_text.stroke-46"),sQuery(id+"F9.wireOp",EDGE,"E15.sketch_text.stroke-47"),sQuery(id+"F9.wireOp",EDGE,"E15.sketch_text.stroke-48"),sQuery(id+"F9.wireOp",EDGE,"E15.sketch_text.stroke-49"),sQuery(id+"F9.wireOp",EDGE,"E15.sketch_text.stroke-50"),sQuery(id+"F9.wireOp",EDGE,"E15.sketch_text.stroke-51"),sQuery(id+"F9.wireOp",EDGE,"E15.sketch_text.stroke-52"),sQuery(id+"F9.wireOp",EDGE,"E15.sketch_text.stroke-53"),sQuery(id+"F9.wireOp",EDGE,"E15.sketch_text.stroke-54")])]});
            var Q6;
            Q6=makeQuery(id+"F1.opExtrude","SWEPT_BODY",BODY,{"disambiguationData":[OSD([sQuery(id+"F0.wireOp",EDGE,"E0.bottom"),sQuery(id+"F0.wireOp",EDGE,"E0.top"),sQuery(id+"F0.wireOp",EDGE,"E0.left"),sQuery(id+"F0.wireOp",EDGE,"E0.right")])]});
            booleanBodies(context, id + "F20", {"operationType" : BooleanOperationType.SUBTRACTION, "tools" : qUnion([Q0, Q1, Q2, Q3, Q4, Q5]), "targets" : qUnion([Q6]), "keepTools" : true});
        }
        {
            var Q0;
            Q0=makeQuery(id+"F12.opExtrude","SWEPT_BODY",BODY,{"disambiguationData":[OSD([sQuery(id+"F11.wireOp",EDGE,"E17.bottom"),sQuery(id+"F11.wireOp",EDGE,"E17.top"),sQuery(id+"F11.wireOp",EDGE,"E17.left"),sQuery(id+"F11.wireOp",EDGE,"E17.right"),sQuery(id+"F11.wireOp",EDGE,"E18.bottom"),sQuery(id+"F11.wireOp",EDGE,"E18.top"),sQuery(id+"F11.wireOp",EDGE,"E18.left"),sQuery(id+"F11.wireOp",EDGE,"E18.right"),sQuery(id+"F11.wireOp",EDGE,"E19.filletArc"),sQuery(id+"F11.wireOp",EDGE,"E20.filletArc"),sQuery(id+"F11.wireOp",EDGE,"E21.filletArc"),sQuery(id+"F11.wireOp",EDGE,"E22.filletArc"),sQuery(id+"F11.wireOp",EDGE,"E23.filletArc"),sQuery(id+"F11.wireOp",EDGE,"E24.filletArc"),sQuery(id+"F11.wireOp",EDGE,"E25.filletArc"),sQuery(id+"F11.wireOp",EDGE,"E26.filletArc")])]});
            var Q1;
            Q1=makeQuery(id+"F1.opExtrude","SWEPT_BODY",BODY,{"disambiguationData":[OSD([sQuery(id+"F0.wireOp",EDGE,"E0.bottom"),sQuery(id+"F0.wireOp",EDGE,"E0.top"),sQuery(id+"F0.wireOp",EDGE,"E0.left"),sQuery(id+"F0.wireOp",EDGE,"E0.right")])]});
            booleanBodies(context, id + "F21", {"operationType" : BooleanOperationType.SUBTRACTION, "tools" : qUnion([Q0]), "targets" : qUnion([Q1]), "keepTools" : true});
        }
        {
            var Q0;
            Q0=qCreatedBy(id+"F2.planeOp",FACE);
            var sketch = newSketch(context, id + "F22", { "sketchPlane" : qUnion([Q0])});
            skCircle(sketch, "E103", {"center": v(-50.15, 33) * mm, "radius": 1.63 * mm});
            skCircle(sketch, "E104.MirrorC", {"center": v(50.15, 33) * mm, "radius": 1.63 * mm});
            skCircle(sketch, "E105.MirrorC", {"center": v(-50.15, -33) * mm, "radius": 1.63 * mm});
            skCircle(sketch, "E106.MirrorC", {"center": v(50.15, -33) * mm, "radius": 1.63 * mm});
            skSolve(sketch);
        }
        {
            var Q0;
            Q0 = qSketchRegion(id + "F22", true);
            extrude(context, id + "F23", {"entities" : qUnion([Q0]), "operationType" : NewBodyOperationType.REMOVE, "endBound" : BoundingType.THROUGH_ALL, "depth" : 25 * mm, "hasSecondDirection" : true, "secondDirectionBound" : SecondDirectionBoundingType.THROUGH_ALL, "secondDirectionOppositeDirection" : true, "secondDirectionDepth" : 25 * mm});
        }
    });
